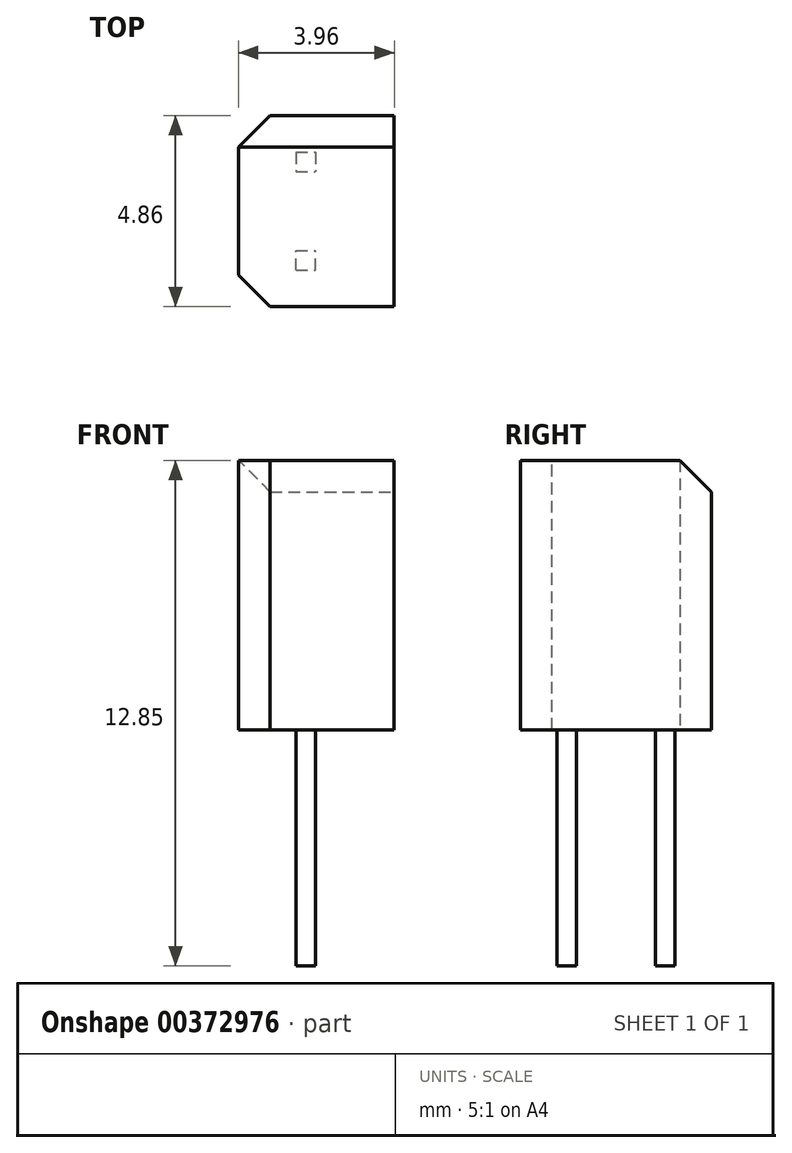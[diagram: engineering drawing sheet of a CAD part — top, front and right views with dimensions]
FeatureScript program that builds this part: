
annotation { "Feature Type Name" : "Feature", "Feature Type Description" : "" }
export const myFeature = defineFeature(function(context is Context, id is Id, definition is map)
    precondition{}
    {
        {
            var Q0;
            Q0=qCreatedBy(makeId("Front.planeOp"),FACE);
            var sketch = newSketch(context, id + "F0", { "sketchPlane" : qUnion([Q0])});
            skLineSegment(sketch, "E0.bottom", {"start": v(-1.98, 0) * mm, "end": v(1.98, 0) * mm});
            skLineSegment(sketch, "E0.top", {"start": v(-1.98, 6.85) * mm, "end": v(1.98, 6.85) * mm});
            skLineSegment(sketch, "E0.left", {"start": v(-1.98, 0) * mm, "end": v(-1.98, 6.85) * mm});
            skLineSegment(sketch, "E0.right", {"start": v(1.98, 0) * mm, "end": v(1.98, 6.85) * mm});
            skSolve(sketch);
        }
        {
            var Q0;
            Q0 = qSketchRegion(id + "F0", true);
            extrude(context, id + "F1", {"entities" : qUnion([Q0]), "depth" : 4.85 * mm, "offsetDistance" : 25 * mm, "symmetric" : true});
        }
        {
            var Q0;
            Q0=makeQuery(id+"F1.opExtrude","CAP_EDGE",EDGE,{"disambiguationData":[OSD([sQuery(id+"F0.wireOp",EDGE,"E0.top")])],"isStart":true});
            var Q1;
            Q1=makeQuery(id+"F1.opExtrude","CAP_EDGE",EDGE,{"disambiguationData":[OSD([sQuery(id+"F0.wireOp",EDGE,"E0.left")])],"isStart":false});
            var Q2;
            Q2=makeQuery(id+"F1.opExtrude","CAP_EDGE",EDGE,{"disambiguationData":[OSD([sQuery(id+"F0.wireOp",EDGE,"E0.left")])],"isStart":true});
            chamfer(context, id + "F2", {"entities" : qUnion([Q0, Q1, Q2]), "width" : 0.8 * mm, "tangentPropagation" : true});
        }
        {
            var Q0;
            Q0=makeQuery(id+"F1.opExtrude","SWEPT_FACE",FACE,{"disambiguationData":[OSD([sQuery(id+"F0.wireOp",EDGE,"E0.bottom")])]});
            var sketch = newSketch(context, id + "F3", { "sketchPlane" : qUnion([Q0])});
            skLineSegment(sketch, "E1", {"start": v(0, 0) * mm, "end": v(-4.93, 0) * mm, "construction": true});
            skLineSegment(sketch, "E2.bottom", {"start": v(-0.52, 1.5) * mm, "end": v(-0.02, 1.5) * mm});
            skLineSegment(sketch, "E2.top", {"start": v(-0.52, 1) * mm, "end": v(-0.02, 1) * mm});
            skLineSegment(sketch, "E2.left", {"start": v(-0.52, 1.5) * mm, "end": v(-0.52, 1) * mm});
            skLineSegment(sketch, "E2.right", {"start": v(-0.02, 1.5) * mm, "end": v(-0.02, 1) * mm});
            skLineSegment(sketch, "E3.MirrorCS", {"start": v(-0.52, -1) * mm, "end": v(-0.02, -1) * mm});
            skLineSegment(sketch, "E4.MirrorCS", {"start": v(-0.52, -1.5) * mm, "end": v(-0.02, -1.5) * mm});
            skLineSegment(sketch, "E5.MirrorCS", {"start": v(-0.52, -1.5) * mm, "end": v(-0.52, -1) * mm});
            skLineSegment(sketch, "E6.MirrorCS", {"start": v(-0.02, -1.5) * mm, "end": v(-0.02, -1) * mm});
            skSolve(sketch);
        }
        {
            var Q0;
            Q0 = qSketchRegion(id + "F3", true);
            extrude(context, id + "F4", {"entities" : qUnion([Q0]), "operationType" : NewBodyOperationType.ADD, "depth" : 6 * mm, "offsetDistance" : 25 * mm});
        }
    });
